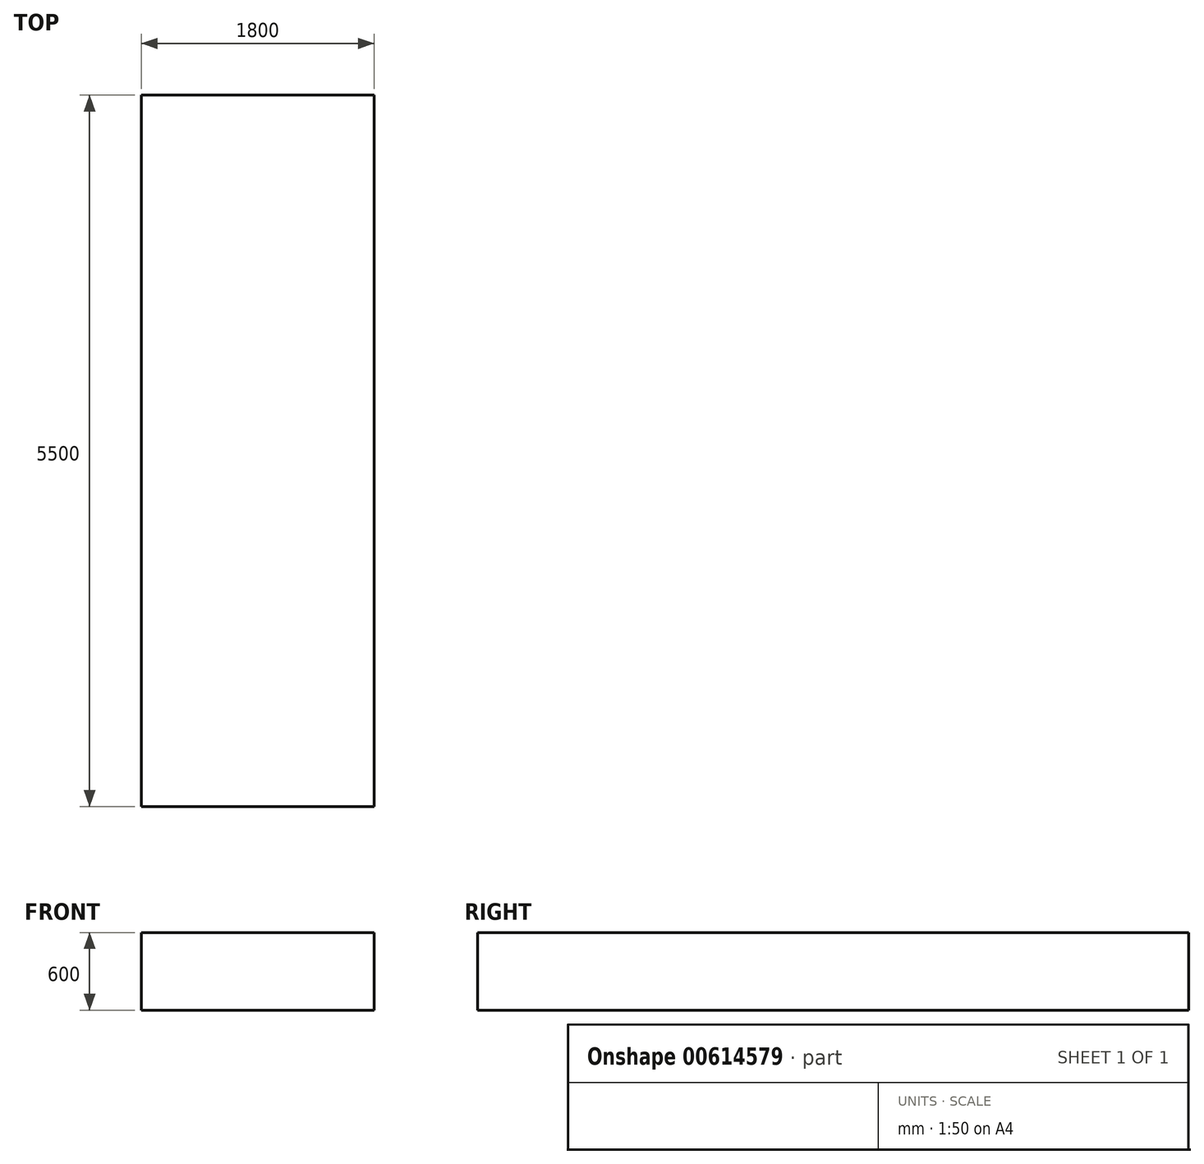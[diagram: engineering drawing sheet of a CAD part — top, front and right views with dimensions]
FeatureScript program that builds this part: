
annotation { "Feature Type Name" : "Feature", "Feature Type Description" : "" }
export const myFeature = defineFeature(function(context is Context, id is Id, definition is map)
    precondition{}
    {
        {
            var Q0;
            Q0=qCreatedBy(makeId("Top.planeOp"),FACE);
            var sketch = newSketch(context, id + "F0", { "sketchPlane" : qUnion([Q0])});
            skLineSegment(sketch, "E0.bottom", {"start": v(-900, 2750) * mm, "end": v(900, 2750) * mm});
            skLineSegment(sketch, "E0.top", {"start": v(-900, -2750) * mm, "end": v(900, -2750) * mm});
            skLineSegment(sketch, "E0.left", {"start": v(-900, 2750) * mm, "end": v(-900, -2750) * mm});
            skLineSegment(sketch, "E0.right", {"start": v(900, 2750) * mm, "end": v(900, -2750) * mm});
            skPoint(sketch, "E0.middle", {"position": v(0, 0) * mm});
            skSolve(sketch);
        }
        {
            var Q0;
            Q0=makeQuery(id+"F0.imprint","IMPRINT",FACE,{"disambiguationData":[TD([[makeQuery(id+"F0.imprint","IMPRINT",EDGE,{"derivedFrom":sQuery(id+"F0.wireOp",EDGE,"E0.bottom")}),-1.0]])]});
            extrude(context, id + "F1", {"entities" : qUnion([Q0]), "depth" : 600 * mm, "offsetDistance" : 25 * mm});
        }
    });
